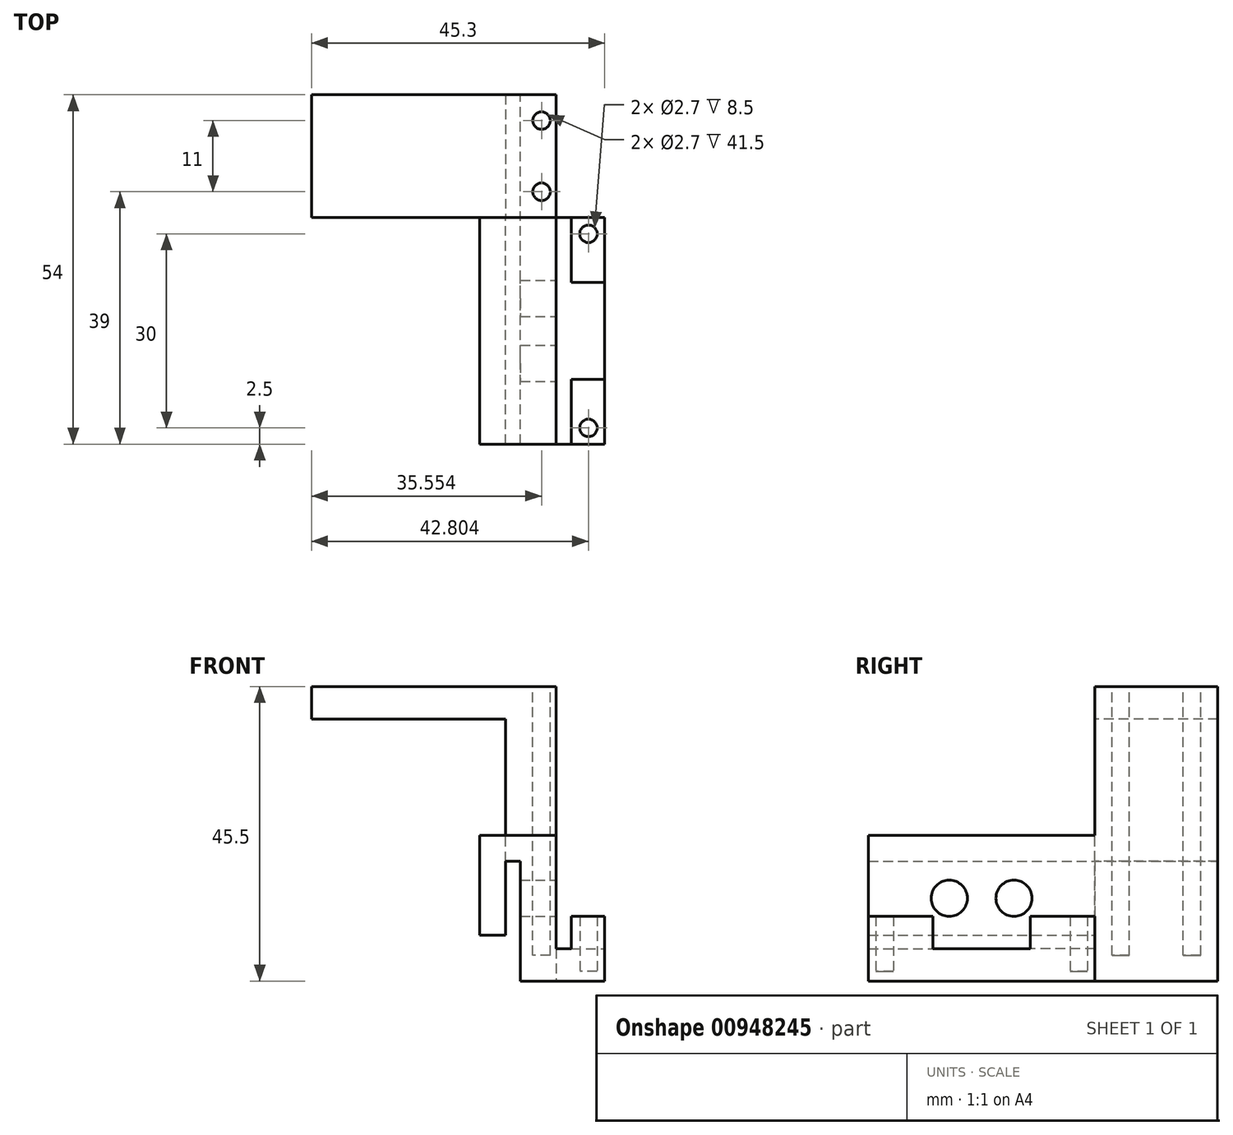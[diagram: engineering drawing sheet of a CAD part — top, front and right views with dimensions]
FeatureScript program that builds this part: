
annotation { "Feature Type Name" : "Feature", "Feature Type Description" : "" }
export const myFeature = defineFeature(function(context is Context, id is Id, definition is map)
    precondition{}
    {
        {
            var Q0;
            Q0=qCreatedBy(makeId("Front.planeOp"),FACE);
            var sketch = newSketch(context, id + "F0", { "sketchPlane" : qUnion([Q0])});
            skLineSegment(sketch, "E0", {"start": v(-36.46, 19.1) * mm, "end": v(-36.46, 34.5) * mm});
            skLineSegment(sketch, "E1", {"start": v(-36.46, 34.5) * mm, "end": v(-24.66, 34.5) * mm});
            skLineSegment(sketch, "E2", {"start": v(-24.66, 34.5) * mm, "end": v(-24.66, 17) * mm});
            skLineSegment(sketch, "E3", {"start": v(-17.16, 12) * mm, "end": v(-30.16, 12) * mm});
            skLineSegment(sketch, "E4", {"start": v(-30.16, 12) * mm, "end": v(-30.16, 30.5) * mm});
            skLineSegment(sketch, "E5", {"start": v(-30.16, 30.5) * mm, "end": v(-32.46, 30.5) * mm});
            skLineSegment(sketch, "E6", {"start": v(-32.46, 30.5) * mm, "end": v(-32.46, 19.1) * mm});
            skLineSegment(sketch, "E7", {"start": v(-32.46, 19.1) * mm, "end": v(-36.46, 19.1) * mm});
            skLineSegment(sketch, "E8", {"start": v(-24.66, 17) * mm, "end": v(-17.16, 17) * mm});
            skLineSegment(sketch, "E9", {"start": v(-17.16, 17) * mm, "end": v(-17.16, 12) * mm});
            skSolve(sketch);
        }
        {
            var Q0;
            Q0=qSketchRegion(id+"F0",true);
            extrude(context, id + "F1", {"entities" : qUnion([Q0]), "depth" : 35 * mm, "offsetDistance" : 25 * mm});
        }
        {
            var Q0;
            Q0=makeQuery(id+"F1.opExtrude","SWEPT_FACE",FACE,{"disambiguationData":[OSD([sQuery(id+"F0.wireOp",EDGE,"E8")])]});
            var sketch = newSketch(context, id + "F2", { "sketchPlane" : qUnion([Q0])});
            skLineSegment(sketch, "E10", {"start": v(-19.66, 0) * mm, "end": v(-19.66, -35) * mm, "construction": true});
            skLineSegment(sketch, "E11", {"start": v(-19.66, -2.5) * mm, "end": v(-17.16, -2.5) * mm, "construction": true});
            skLineSegment(sketch, "E12", {"start": v(-19.66, -32.5) * mm, "end": v(-17.16, -32.5) * mm, "construction": true});
            skLineSegment(sketch, "E13.bottom", {"start": v(-22.34, 0) * mm, "end": v(-17.16, 0) * mm});
            skLineSegment(sketch, "E13.top", {"start": v(-22.34, -10) * mm, "end": v(-17.16, -10) * mm});
            skLineSegment(sketch, "E13.left", {"start": v(-22.34, 0) * mm, "end": v(-22.34, -10) * mm});
            skLineSegment(sketch, "E13.right", {"start": v(-17.16, 0) * mm, "end": v(-17.16, -10) * mm});
            skLineSegment(sketch, "E14.bottom", {"start": v(-22.34, -35) * mm, "end": v(-17.16, -35) * mm});
            skLineSegment(sketch, "E14.top", {"start": v(-22.34, -25) * mm, "end": v(-17.16, -25) * mm});
            skLineSegment(sketch, "E14.left", {"start": v(-22.34, -35) * mm, "end": v(-22.34, -25) * mm});
            skLineSegment(sketch, "E14.right", {"start": v(-17.16, -35) * mm, "end": v(-17.16, -25) * mm});
            skCircle(sketch, "E15", {"center": v(-19.66, -32.5) * mm, "radius": 1.35 * mm});
            skCircle(sketch, "E16", {"center": v(-19.66, -2.5) * mm, "radius": 1.35 * mm});
            skSolve(sketch);
        }
        {
            var Q0;
            Q0=qSketchRegion(id+"F2",true);
            extrude(context, id + "F3", {"entities" : qUnion([Q0]), "operationType" : NewBodyOperationType.ADD, "depth" : 5 * mm, "offsetDistance" : 25 * mm});
        }
        {
            var Q0;
            Q0=makeQuery(id+"F1.opExtrude","SWEPT_FACE",FACE,{"disambiguationData":[OSD([sQuery(id+"F0.wireOp",EDGE,"E2")])]});
            var sketch = newSketch(context, id + "F4", { "sketchPlane" : qUnion([Q0])});
            skLineSegment(sketch, "E17", {"start": v(-35, 24.8) * mm, "end": v(0, 24.8) * mm, "construction": true});
            skLineSegment(sketch, "E18", {"start": v(-22.5, 24.8) * mm, "end": v(-22.5, 34.5) * mm, "construction": true});
            skLineSegment(sketch, "E19", {"start": v(-12.5, 24.8) * mm, "end": v(-12.5, 34.5) * mm, "construction": true});
            skCircle(sketch, "E20", {"center": v(-22.5, 24.8) * mm, "radius": 2.8 * mm});
            skCircle(sketch, "E21", {"center": v(-22.5, 24.8) * mm, "radius": 3.83 * mm});
            skCircle(sketch, "E22", {"center": v(-12.5, 24.8) * mm, "radius": 2.8 * mm});
            skCircle(sketch, "E23", {"center": v(-12.5, 24.8) * mm, "radius": 3.83 * mm});
            skSolve(sketch);
        }
        {
            var Q0;
            Q0=makeQuery(id+"F4.imprint","IMPRINT",FACE,{"disambiguationData":[TD([[makeQuery(id+"F4.imprint","IMPRINT",EDGE,{"derivedFrom":sQuery(id+"F4.wireOp",EDGE,"E20")}),1.0]])]});
            var Q1;
            Q1=makeQuery(id+"F4.imprint","IMPRINT",FACE,{"disambiguationData":[TD([[makeQuery(id+"F4.imprint","IMPRINT",EDGE,{"derivedFrom":sQuery(id+"F4.wireOp",EDGE,"E22")}),1.0]])]});
            extrude(context, id + "F5", {"entities" : qUnion([Q0, Q1]), "operationType" : NewBodyOperationType.REMOVE, "endBound" : BoundingType.UP_TO_NEXT, "oppositeDirection" : true, "depth" : 5.7 * mm, "offsetDistance" : 25 * mm});
        }
        {
            var Q0;
            Q0=makeQuery(id+"F1.opExtrude","CAP_FACE",FACE,{"disambiguationData":[OSD([sQuery(id+"F0.wireOp",EDGE,"E0"),sQuery(id+"F0.wireOp",EDGE,"E1"),sQuery(id+"F0.wireOp",EDGE,"E2"),sQuery(id+"F0.wireOp",EDGE,"E3"),sQuery(id+"F0.wireOp",EDGE,"E4"),sQuery(id+"F0.wireOp",EDGE,"E5"),sQuery(id+"F0.wireOp",EDGE,"E6"),sQuery(id+"F0.wireOp",EDGE,"E7"),sQuery(id+"F0.wireOp",EDGE,"E8"),sQuery(id+"F0.wireOp",EDGE,"E9")])],"isStart":true});
            var sketch = newSketch(context, id + "F6", { "sketchPlane" : qUnion([Q0])});
            skLineSegment(sketch, "E24", {"start": v(30.16, 12) * mm, "end": v(30.16, 30.5) * mm});
            skLineSegment(sketch, "E25", {"start": v(32.46, 52.5) * mm, "end": v(62.46, 52.5) * mm});
            skLineSegment(sketch, "E26", {"start": v(62.46, 52.5) * mm, "end": v(62.46, 57.5) * mm});
            skLineSegment(sketch, "E27", {"start": v(62.46, 57.5) * mm, "end": v(24.66, 57.5) * mm});
            skLineSegment(sketch, "E28", {"start": v(24.66, 57.5) * mm, "end": v(24.66, 12) * mm});
            skLineSegment(sketch, "E29", {"start": v(24.66, 12) * mm, "end": v(30.16, 12) * mm});
            skLineSegment(sketch, "E30", {"start": v(30.16, 30.5) * mm, "end": v(26.05, 30.5) * mm, "construction": true});
            skLineSegment(sketch, "E31", {"start": v(32.46, 34.5) * mm, "end": v(32.46, 30.5) * mm});
            skLineSegment(sketch, "E32", {"start": v(32.46, 30.5) * mm, "end": v(30.16, 30.5) * mm});
            skLineSegment(sketch, "E33", {"start": v(32.46, 34.5) * mm, "end": v(32.46, 52.5) * mm});
            skPoint(sketch, "E34.orphan", {"position": v(30.16, 52.5) * mm});
            skSolve(sketch);
        }
        {
            var Q0;
            Q0 = qSketchRegion(id + "F6", true);
            extrude(context, id + "F7", {"entities" : qUnion([Q0]), "operationType" : NewBodyOperationType.ADD, "depth" : 19 * mm, "offsetDistance" : 25 * mm});
        }
        {
            var Q0;
            Q0=makeQuery(id+"F7.opExtrude","SWEPT_FACE",FACE,{"disambiguationData":[OSD([sQuery(id+"F6.wireOp",EDGE,"E27")])]});
            var sketch = newSketch(context, id + "F8", { "sketchPlane" : qUnion([Q0])});
            skLineSegment(sketch, "E35", {"start": v(-26.9, 0) * mm, "end": v(-26.9, 19) * mm, "construction": true});
            skCircle(sketch, "E36", {"center": v(-26.9, 4) * mm, "radius": 1.35 * mm});
            skCircle(sketch, "E37", {"center": v(-26.9, 15) * mm, "radius": 1.35 * mm});
            skSolve(sketch);
        }
        {
            var Q0;
            Q0=makeQuery(id+"F8.imprint","IMPRINT",FACE,{"disambiguationData":[TD([[makeQuery(id+"F8.imprint","IMPRINT",EDGE,{"derivedFrom":sQuery(id+"F8.wireOp",EDGE,"E36")}),1.0]])]});
            var Q1;
            Q1=makeQuery(id+"F8.imprint","IMPRINT",FACE,{"disambiguationData":[TD([[makeQuery(id+"F8.imprint","IMPRINT",EDGE,{"derivedFrom":sQuery(id+"F8.wireOp",EDGE,"E37")}),1.0]])]});
            extrude(context, id + "F9", {"entities" : qUnion([Q0, Q1]), "operationType" : NewBodyOperationType.REMOVE, "oppositeDirection" : true, "depth" : 41.5 * mm, "offsetDistance" : 25 * mm});
        }
        {
            var Q0;
            Q0=makeQuery(id+"F3.boolean.opBoolean","SPLIT",FACE,{"disambiguationData":[TD([makeQuery(id+"F3.opExtrude","SWEPT_FACE",FACE,{"disambiguationData":[OSD([sQuery(id+"F2.wireOp",EDGE,"E15")])]})])],"derivedFrom":makeQuery(id+"F1.opExtrude","SWEPT_FACE",FACE,{"disambiguationData":[OSD([sQuery(id+"F0.wireOp",EDGE,"E8")])]})});
            var Q1;
            Q1=makeQuery(id+"F3.boolean.opBoolean","SPLIT",FACE,{"disambiguationData":[TD([makeQuery(id+"F3.opExtrude","SWEPT_FACE",FACE,{"disambiguationData":[OSD([sQuery(id+"F2.wireOp",EDGE,"E16")])]})])],"derivedFrom":makeQuery(id+"F1.opExtrude","SWEPT_FACE",FACE,{"disambiguationData":[OSD([sQuery(id+"F0.wireOp",EDGE,"E8")])]})});
            extrude(context, id + "F10", {"entities" : qUnion([Q0, Q1]), "operationType" : NewBodyOperationType.REMOVE, "oppositeDirection" : true, "depth" : 3.5 * mm, "offsetDistance" : 25 * mm});
        }
    });
